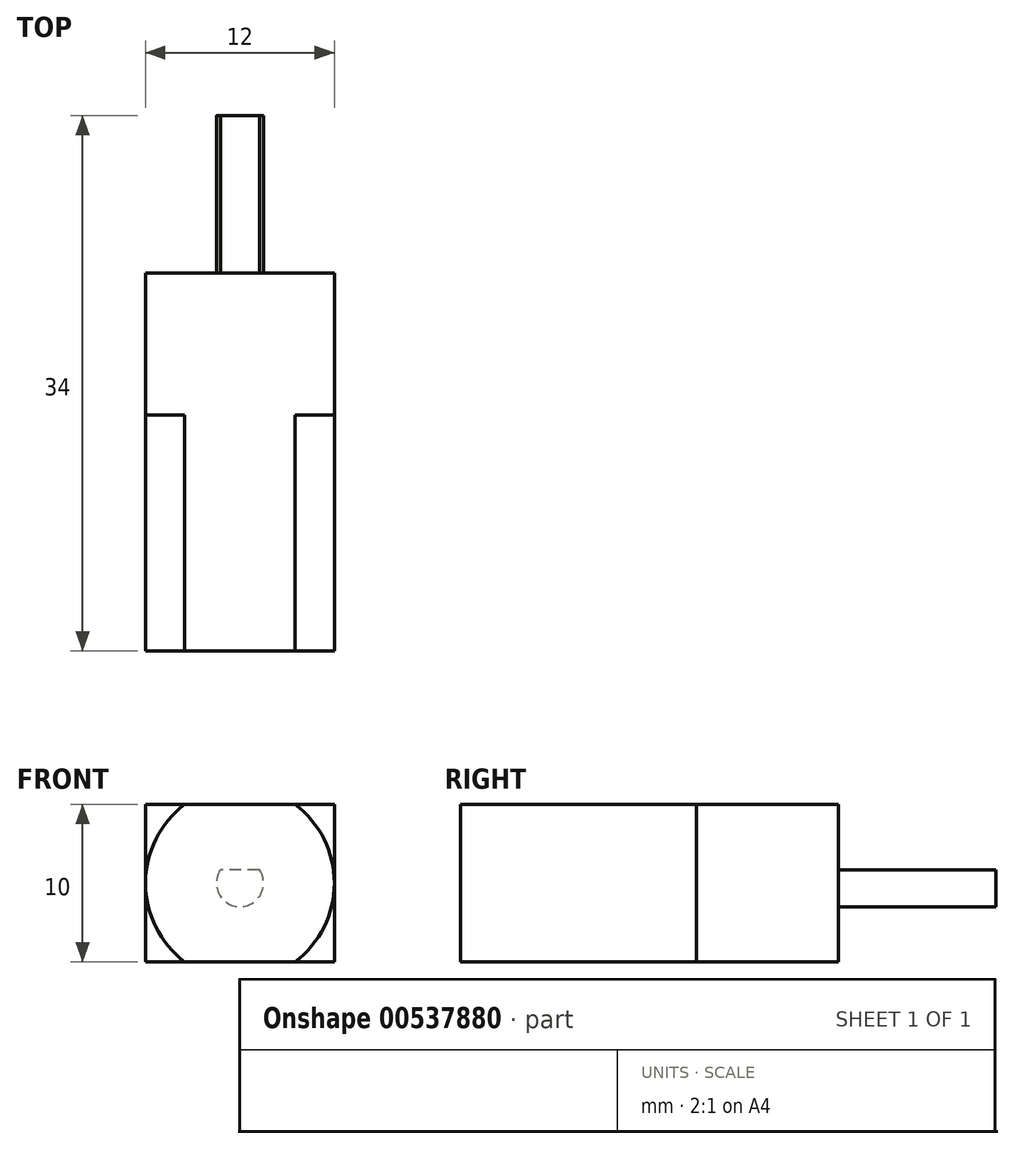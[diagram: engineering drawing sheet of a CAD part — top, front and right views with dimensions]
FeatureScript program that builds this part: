
annotation { "Feature Type Name" : "Feature", "Feature Type Description" : "" }
export const myFeature = defineFeature(function(context is Context, id is Id, definition is map)
    precondition{}
    {
        {
            var Q0;
            Q0=qCreatedBy(makeId("Front.planeOp"),FACE);
            var sketch = newSketch(context, id + "F0", { "sketchPlane" : qUnion([Q0])});
            skLineSegment(sketch, "E0", {"start": v(-3.5, 5) * mm, "end": v(3.5, 5) * mm});
            skLineSegment(sketch, "E1", {"start": v(-3.5, -5) * mm, "end": v(3.5, -5) * mm});
            skArc(sketch, "E2", {"start": v(-3.5, 5) * mm, "mid": v(-6, 0) * mm, "end": v(-3.5, -5) * mm});
            skArc(sketch, "E3", {"start": v(3.5, -5) * mm, "mid": v(6, 0) * mm, "end": v(3.5, 5) * mm});
            skPoint(sketch, "E4", {"position": v(-6, 0) * mm});
            skPoint(sketch, "E5", {"position": v(6, 0) * mm});
            skSolve(sketch);
        }
        {
            var Q0;
            Q0=makeQuery(id+"F0.imprint","IMPRINT",FACE,{"disambiguationData":[TD([[makeQuery(id+"F0.imprint","IMPRINT",EDGE,{"derivedFrom":sQuery(id+"F0.wireOp",EDGE,"E0")}),-1.0]])]});
            extrude(context, id + "F1", {"entities" : qUnion([Q0]), "depth" : 15 * mm, "offsetDistance" : 25 * mm});
        }
        {
            var Q0;
            Q0=makeQuery(id+"F1.opExtrude","CAP_FACE",FACE,{"disambiguationData":[OSD([sQuery(id+"F0.wireOp",EDGE,"E0"),sQuery(id+"F0.wireOp",EDGE,"E1"),sQuery(id+"F0.wireOp",EDGE,"E2"),sQuery(id+"F0.wireOp",EDGE,"E3")])],"isStart":true});
            var sketch = newSketch(context, id + "F2", { "sketchPlane" : qUnion([Q0])});
            skPoint(sketch, "E6.0", {"position": v(6, 0) * mm});
            skPoint(sketch, "E7.0", {"position": v(-6, 0) * mm});
            skPoint(sketch, "E8.0", {"position": v(0, 5) * mm});
            skPoint(sketch, "E9.0", {"position": v(0, -5) * mm});
            skLineSegment(sketch, "E10.bottom", {"start": v(6, 5) * mm, "end": v(-6, 5) * mm});
            skLineSegment(sketch, "E10.top", {"start": v(6, -5) * mm, "end": v(-6, -5) * mm});
            skLineSegment(sketch, "E10.left", {"start": v(6, 5) * mm, "end": v(6, -5) * mm});
            skLineSegment(sketch, "E10.right", {"start": v(-6, 5) * mm, "end": v(-6, -5) * mm});
            skSolve(sketch);
        }
        {
            var Q0;
            Q0 = qSketchRegion(id + "F2", true);
            extrude(context, id + "F3", {"entities" : qUnion([Q0]), "operationType" : NewBodyOperationType.ADD, "depth" : 9 * mm, "offsetDistance" : 25 * mm});
        }
        {
            var Q0;
            Q0=makeQuery(id+"F3.opExtrude","CAP_FACE",FACE,{"disambiguationData":[OSD([sQuery(id+"F2.wireOp",EDGE,"E10.bottom"),sQuery(id+"F2.wireOp",EDGE,"E10.top"),sQuery(id+"F2.wireOp",EDGE,"E10.left"),sQuery(id+"F2.wireOp",EDGE,"E10.right")])],"isStart":false});
            var sketch = newSketch(context, id + "F4", { "sketchPlane" : qUnion([Q0])});
            skLineSegment(sketch, "E11", {"start": v(0, 0.9) * mm, "end": v(0, 0.9) * mm});
            skArc(sketch, "E12", {"start": v(-1.24, 0.85) * mm, "mid": v(0, -1.5) * mm, "end": v(1.24, 0.85) * mm});
            skLineSegment(sketch, "E13", {"start": v(-1.24, 0.85) * mm, "end": v(1.24, 0.85) * mm});
            skPoint(sketch, "E14", {"position": v(0, -1.5) * mm});
            skSolve(sketch);
        }
        {
            var Q0;
            Q0 = qSketchRegion(id + "F4", true);
            extrude(context, id + "F5", {"entities" : qUnion([Q0]), "operationType" : NewBodyOperationType.ADD, "depth" : 10 * mm, "offsetDistance" : 25 * mm});
        }
    });
